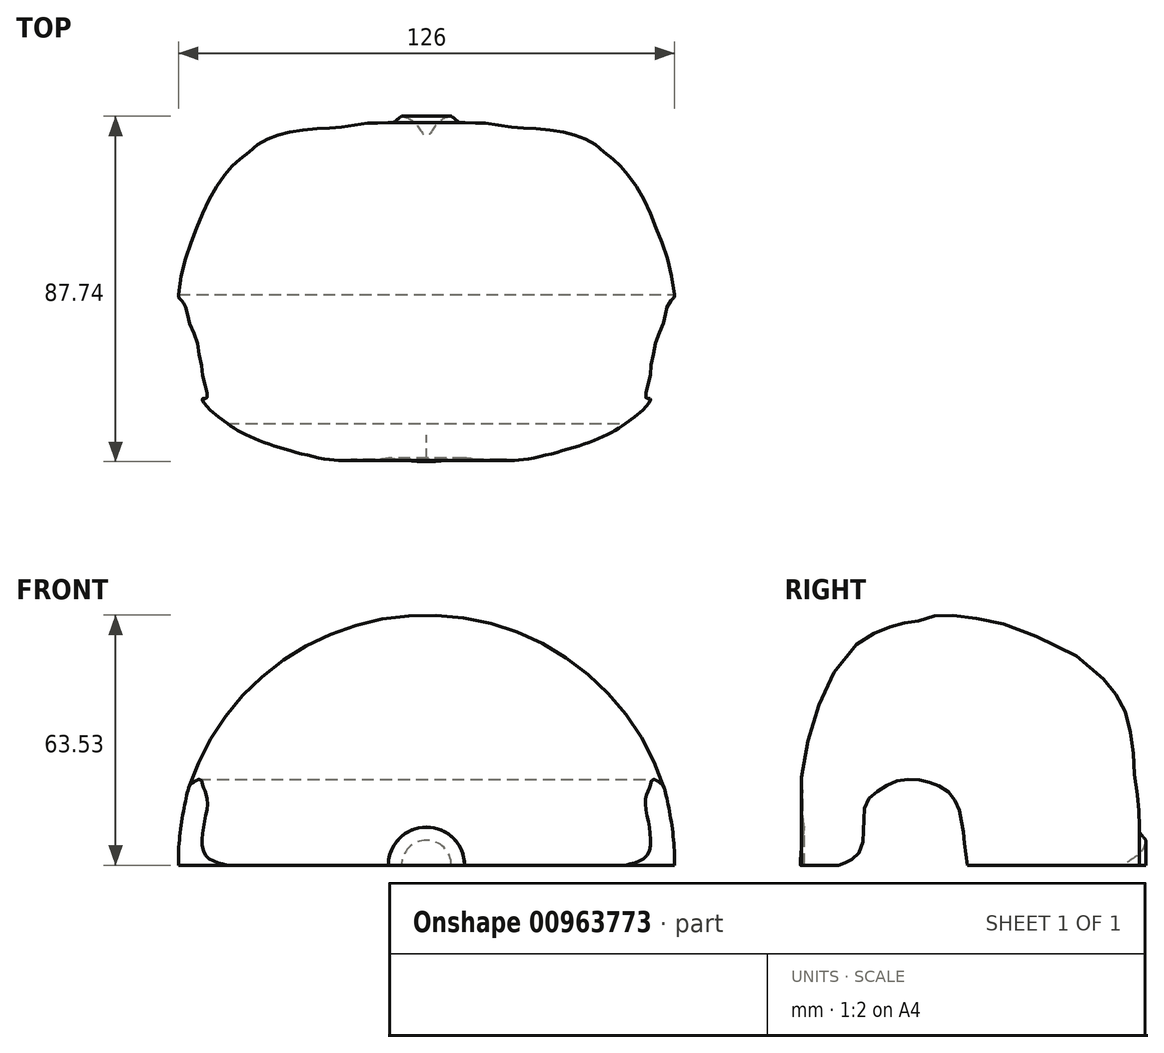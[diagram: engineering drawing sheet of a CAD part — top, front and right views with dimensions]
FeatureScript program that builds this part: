
annotation { "Feature Type Name" : "Feature", "Feature Type Description" : "" }
export const myFeature = defineFeature(function(context is Context, id is Id, definition is map)
    precondition{}
    {
        {
            var Q0;
            Q0=qCreatedBy(makeId("Right.planeOp"),FACE);
            var sketch = newSketch(context, id + "F0", { "sketchPlane" : qUnion([Q0])});
            skFitSpline(sketch, "E0", {"points": [v(25.97, 0) * mm, v(24.4, 2.13) * mm, v(24.4, 2.97) * mm, v(24.29, 5.76) * mm, v(24.2, 8.68) * mm, v(23.48, 13.73) * mm, v(23.01, 18.2) * mm, v(22.73, 22.94) * mm, v(21.9, 28.52) * mm, v(20.87, 32.24) * mm, v(19.38, 35.78) * mm, v(16.96, 38.66) * mm, v(14.73, 41.54) * mm, v(12.39, 43.8) * mm, v(8.18, 46.95) * mm, v(2.39, 50.11) * mm, v(-4.19, 52.74) * mm, v(-11.82, 55.37) * mm, v(-21.54, 56.92) * mm, v(-26.94, 57.11) * mm, v(-29.35, 56.37) * mm, v(-32.52, 55.62) * mm, v(-35.12, 55.25) * mm, v(-36.89, 54.7) * mm, v(-39.21, 54.23) * mm, v(-42.56, 52.83) * mm, v(-46.19, 50.79) * mm, v(-48.98, 48.27) * mm, v(-51.21, 45.4) * mm, v(-54.1, 41.2) * mm, v(-57.07, 34.32) * mm, v(-59.95, 24.65) * mm, v(-61.44, 15.9) * mm, v(-61.16, 12.93) * mm, v(-61.35, 10.51) * mm, v(-60.98, 4.75) * mm, v(-60.8, 3.35) * mm, v(-60.8, 3.44) * mm], "startDerivative": vector(-51.3, 94.6) * mm, "endDerivative": vector(-1.1, 32.54) * mm});
            skLineSegment(sketch, "E1", {"start": v(-54.97, -6.32) * mm, "end": v(20.3, -6.32) * mm});
            skFitSpline(sketch, "E2", {"points": [v(-60.8, 3.35) * mm, v(-61.24, 0) * mm, v(-61.7, -4.25) * mm, v(-61.77, -6.3) * mm], "startDerivative": vector(-1.28, -9.16) * mm, "endDerivative": vector(-0.11, -6.82) * mm});
            skLineSegment(sketch, "E3", {"start": v(-61.77, -6.3) * mm, "end": v(-54.97, -6.32) * mm});
            skFitSpline(sketch, "E4", {"points": [v(25.97, 0) * mm, v(24.85, -2.82) * mm, v(21.73, -5.28) * mm, v(20.3, -6.32) * mm], "startDerivative": vector(-1.87, -8.54) * mm, "endDerivative": vector(-4.65, -3.6) * mm});
            skPoint(sketch, "E5.orphan", {"position": v(25.64, -6.32) * mm});
            skSolve(sketch);
        }
        {
            var Q0;
            {var subQ3=sQuery(id+"F0.wireOp",EDGE,"9d046740-f6ee-489e-9ff4-2169ff36ba79");Q0=makeQuery(id+"F0.imprint","IMPRINT",FACE,{"disambiguationData":[TD([[makeQuery(id+"F0.imprint","IMPRINT",EDGE,{"derivedFrom":subQ3}),1.0]])]});}
            var Q1;
            {var subQ0=sQuery(id+"F0.wireOp",EDGE,"E2");Q1=makeQuery(id+"F0.imprint","IMPRINT",FACE,{"disambiguationData":[TD([[makeQuery(id+"F0.imprint","IMPRINT",EDGE,{"derivedFrom":subQ0}),1.0]])]});}
            var Q2;
            Q2=sQuery(id+"F0.wireOp",EDGE,"E1");
            revolve(context, id + "F1", {"surfaceOperationType" : NewSurfaceOperationType.NEW, "entities" : qUnion([Q0, Q1]), "axis" : qUnion([Q2]), "revolveType" : RevolveType.SYMMETRIC, "angle" : 180 * degree});
        }
        {
            var Q0;
            Q0=qCreatedBy(makeId("Right.planeOp"),FACE);
            var sketch = newSketch(context, id + "F2", { "sketchPlane" : qUnion([Q0])});
            skFitSpline(sketch, "E6", {"points": [v(-55.84, -7.35) * mm, v(-48.65, -4.85) * mm, v(-46.14, -1.4) * mm, v(-45.68, 5.47) * mm, v(-44.9, 9.85) * mm, v(-41.45, 12.98) * mm, v(-35.98, 15.33) * mm, v(-27.84, 14.39) * mm, v(-23, 10.95) * mm, v(-20.96, 5.63) * mm, v(-20.18, 0) * mm, v(-20.02, -1.72) * mm, v(-19.55, -7.98) * mm, v(-21.43, -8.3) * mm], "startDerivative": vector(86.94, 22.2) * mm, "endDerivative": vector(-49.3, 9.42) * mm});
            skLineSegment(sketch, "E7", {"start": v(-55.84, -7.35) * mm, "end": v(-21.43, -8.3) * mm});
            skSolve(sketch);
        }
        {
            var Q0;
            Q0 = qSketchRegion(id + "F2", true);
            extrude(context, id + "F3", {"entities" : qUnion([Q0]), "operationType" : NewBodyOperationType.REMOVE, "endBound" : BoundingType.SYMMETRIC, "oppositeDirection" : true, "depth" : 269.24 * mm, "offsetDistance" : 25.4 * mm});
        }
    });
